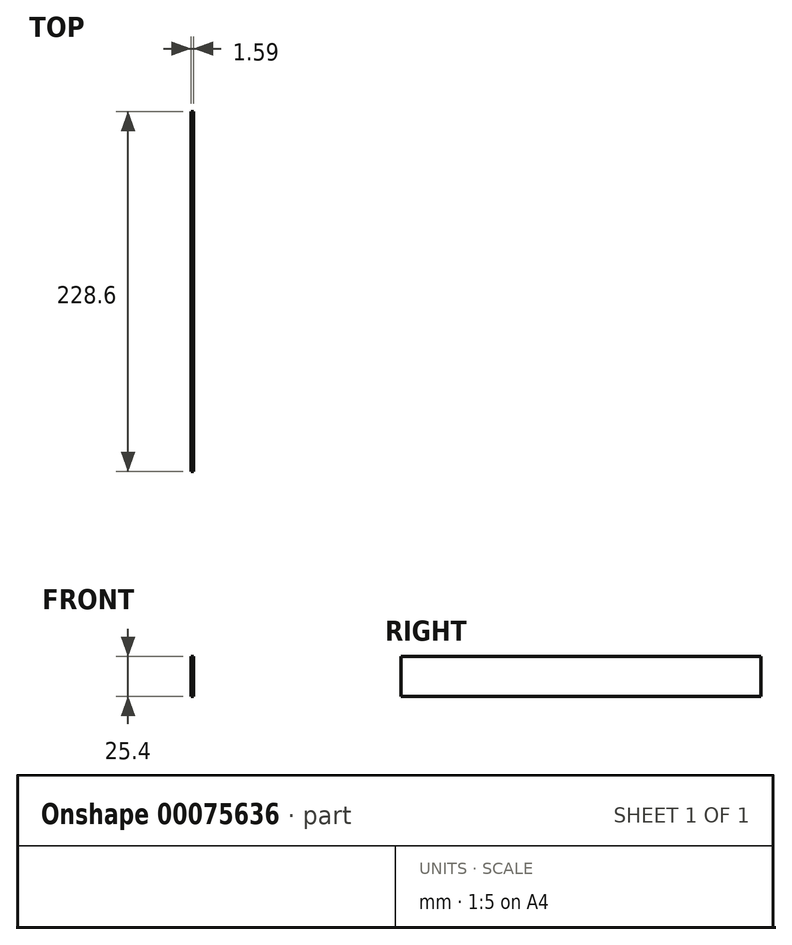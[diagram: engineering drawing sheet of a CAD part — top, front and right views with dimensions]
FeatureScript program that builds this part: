
annotation { "Feature Type Name" : "Feature", "Feature Type Description" : "" }
export const myFeature = defineFeature(function(context is Context, id is Id, definition is map)
    precondition{}
    {
        {
            var Q0;
            Q0=qCreatedBy(makeId("Front.planeOp"),FACE);
            var sketch = newSketch(context, id + "F0", { "sketchPlane" : qUnion([Q0])});
            skLineSegment(sketch, "E0.bottom", {"start": v(0, 0) * mm, "end": v(1.59, 0) * mm});
            skLineSegment(sketch, "E0.top", {"start": v(0, 25.4) * mm, "end": v(1.59, 25.4) * mm});
            skLineSegment(sketch, "E0.left", {"start": v(0, 0) * mm, "end": v(0, 25.4) * mm});
            skLineSegment(sketch, "E0.right", {"start": v(1.59, 0) * mm, "end": v(1.59, 25.4) * mm});
            skSolve(sketch);
        }
        {
            var Q0;
            Q0 = qSketchRegion(id + "F0", true);
            extrude(context, id + "F1", {"entities" : qUnion([Q0]), "depth" : 228.6 * mm});
        }
    });
